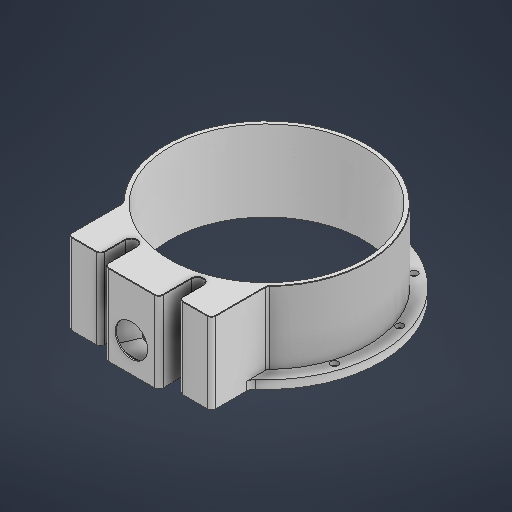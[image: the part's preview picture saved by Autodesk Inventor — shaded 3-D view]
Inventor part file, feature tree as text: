
AUTODESK INVENTOR PART (.ipt)
format: ipt  version: 2025 (Build 290162000, 162)  size: 694,272 bytes
history: native  units: in
note: dims shown in document units (in); Inventor stores cm internally (conversion verified against a paired STEP export)
features: extrude x20, sketch x14, fillet x9, other x3, chamfer x2, plane x1
ambient origin geometry x8: Origin, YZ Plane, XZ Plane, XY Plane, X Axis, Y Axis, Z Axis, Center Point
bodies: Body1 (feature_tree)
feature tree (49):
  other  "Cylinder.ipt"
  extrude  "Extrusion1"  Depth=0.3937in
  extrude  "Extrusion2"  Depth=0.3937in TaperAngle=0.0deg
  sketch  "Sketch3"  dims[d7=11.2205in d8=10.6299in]
  extrude  "Extrusion3"  Depth=10.6299in
  extrude  "Extrusion5"  Depth=0.1969in TaperAngle=0.0deg
  sketch  "Sketch6"  dims[d24=0.1969in d25=0.0in d31=0.0in d32=0.0in]
  extrude  "Extrusion6"  Depth=0.2953in
  extrude  "Extrusion7"  TaperAngle=0.0deg  [1 undecoded]
  extrude  "Extrusion8"  Depth=9.8425in
  plane  "Work Plane1"
  extrude  "Extrusion9"  Depth=9.065in
  extrude  "Extrusion21"  Depth=0.3937in
  sketch  "Sketch18"  dims[d107=2.2047in d108=0.0in d111=3.937in d112=0.0in]
  extrude  "Extrusion22"  Depth=3.937in TaperAngle=0.0deg
  sketch  "Sketch19"  dims[d113=2.5591in d115=2.2047in d116=0.0in]
  extrude  "Extrusion23"  Depth=2.2047in TaperAngle=0.0deg
  extrude  "Extrusion27"  Depth=0.5433in
  extrude  "Extrusion31"  Depth=9.4488in
  extrude  "Extrusion32"  Depth=0.3937in TaperAngle=0.0deg
  extrude  "Extrusion33"  TaperAngle=0.0deg  [1 undecoded]
  extrude  "Extrusion34"  Depth=0.3937in
  fillet  "Fillet9"  Radius=0.0787in
  fillet  "Fillet10"  Radius=1.8325in
  fillet  "Fillet11"  [1 undecoded]
  fillet  "Fillet12"  Radius=2.2047in
  chamfer  "Chamfer5"  Distance=4.1339in
  extrude  "Extrusion36"  Depth=0.3937in TaperAngle=0.0deg
  fillet  "Fillet13"  Radius=0.0787in
  chamfer  "Chamfer6"  Distance=0.3937in
  fillet  "Fillet15"  Radius=0.0787in
  fillet  "Fillet16"  Radius=0.1969in
  fillet  "Fillet17"  Radius=0.1969in
  fillet  "Fillet18"  Radius=0.0197in
  extrude  "Extrusion38"  Depth=0.3937in TaperAngle=0.0deg
  extrude  "Extrusion39"  Depth=0.1969in
  extrude  "Extrusion40"  Depth=0.3937in TaperAngle=45.0deg
  other  "Solid12::Cylinder.ipt"
  other  "TaggingFeature1"
  sketch  "Sketch1"  dims[d0=0.3937in d2=10.2362in]
  sketch  "Sketch2"  dims[d3=0.0in d4=0.0in d5=0.3937in d6=0.0in]
  sketch  "Sketch5"  dims[d17=10.6299in d18=0.2953in]
  sketch  "Sketch7"  dims[d33=2.1654in d34=0.0in d35=9.8425in]
  sketch  "Sketch9"  dims[d36=10.6299in d46=9.065in]
  sketch  "Sketch14"  dims[d47=0.3937in d48=0.0in d88=0.0787in]
  sketch  "Sketch22"  dims[d117=0.0591in d119=0.5433in]
  sketch  "Sketch24"  dims[d120=0.5433in d122=9.4488in]
  sketch  "Sketch Circular Pattern3"  dims[d10=0.1969in d11=0.0in d15=0.1969in d16=0.0in]
  sketch  "Sketch26"  dims[d134=0.0787in d141=0.3937in d142=0.0in d159=0.0in d160=0.0in d164=1.5298in d165=0.0787in d166=1.8325in d167=90.0deg d169=2.2047in d170=0.0in d171=4.1339in d172=0.0in d173=1.1614in d174=0.0in d175=0.0787in d177=0.3937in d178=0.0787in d179=0.1969in d180=0.1969in d184=0.0197in d185=0.0787in d186=45.0deg d189=1.9291in d190=0.0in d193=0.1969in d195=0.3912in d196=1.2662in d197=45.0deg d198=0.1969in d199=0.1969in d200=0.1969in d206=0.3937in d207=1.5157in d208=1.378in d209=0.2165in d210=0.3425in d211=3.937in d213=360.0deg d215=0.1181in d216=0.0in d217=10.4151in d218=9.065in d219=6.1806in d220=0.0in d221=0.3937in d222=0.0in d223=0.5433in d224=1.8228in d225=3.5433in d226=2.564in d227=2.7608in d228=3.5433in d143=0.0197in d144=0.0344in d145=0.0197in d146=0.0344in d153=0.0in d154=0.0in d155=0.0in d156=0.0in d201=0.0197in d202=0.0344in d203=0.0197in d204=0.0344in]
note: 3 required parameter values undecoded (feature->parameter linkage not recoverable at this tier; creation-order binding heuristic only, values carry confidence <= 0.55)
